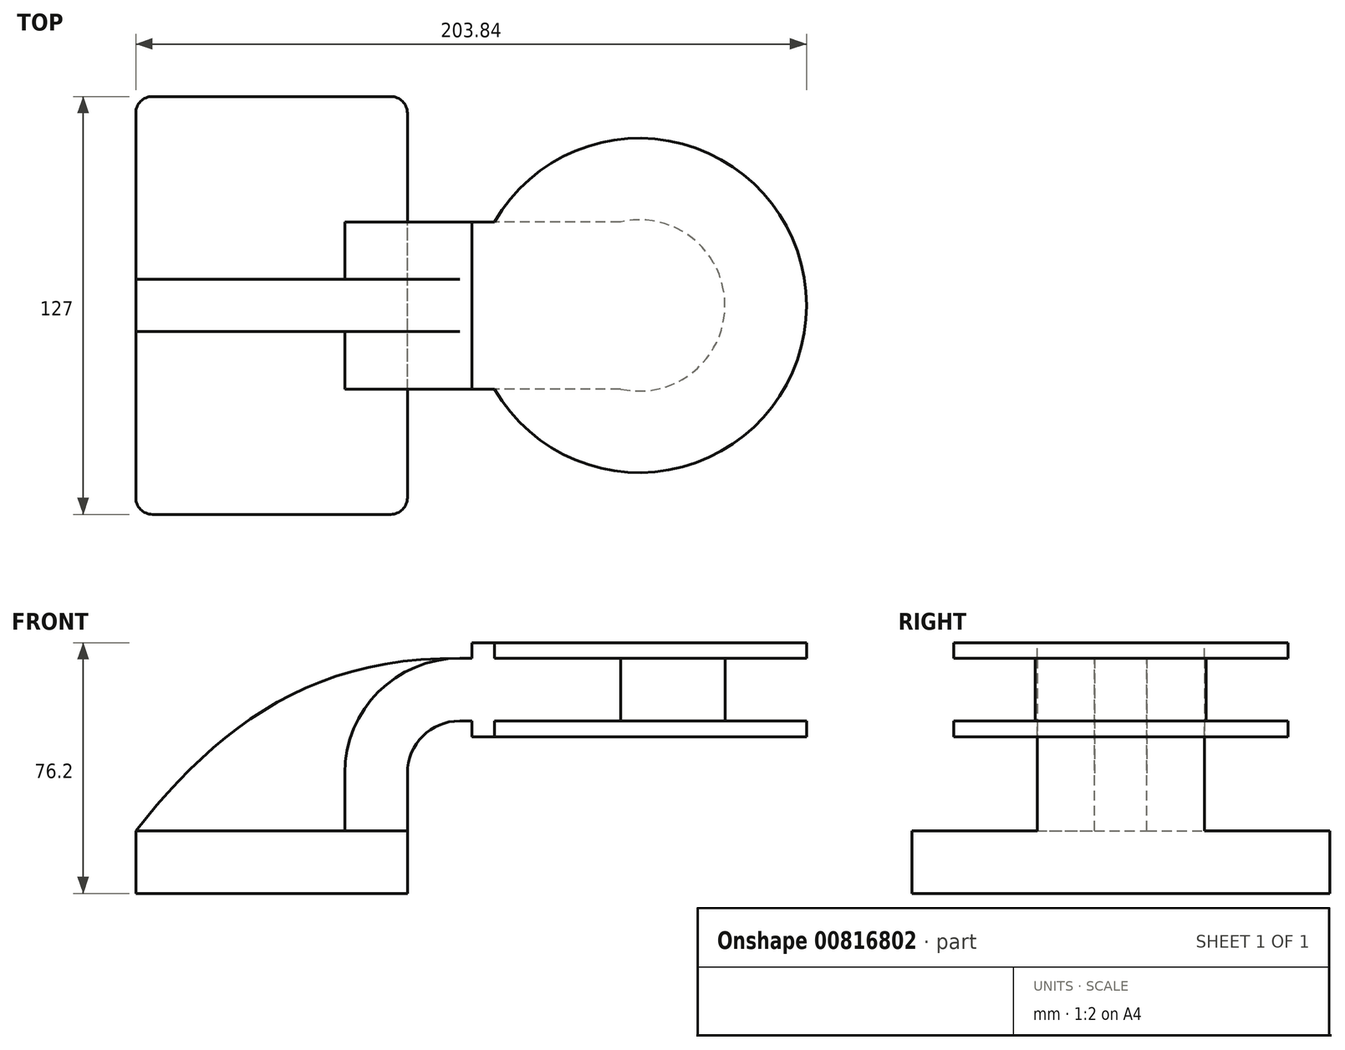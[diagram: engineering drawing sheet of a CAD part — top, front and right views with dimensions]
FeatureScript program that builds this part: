
annotation { "Feature Type Name" : "Feature", "Feature Type Description" : "" }
export const myFeature = defineFeature(function(context is Context, id is Id, definition is map)
    precondition{}
    {
        {
            var Q0;
            Q0=qCreatedBy(makeId("Front.planeOp"),FACE);
            var sketch = newSketch(context, id + "F0", { "sketchPlane" : qUnion([Q0])});
            skLineSegment(sketch, "E0.bottom", {"start": v(-41.28, 9.52) * mm, "end": v(41.27, 9.53) * mm});
            skLineSegment(sketch, "E0.top", {"start": v(-41.28, -9.53) * mm, "end": v(41.28, -9.53) * mm});
            skLineSegment(sketch, "E0.left", {"start": v(-41.28, 9.52) * mm, "end": v(-41.27, -9.53) * mm});
            skLineSegment(sketch, "E0.right", {"start": v(41.28, 9.53) * mm, "end": v(41.28, -9.52) * mm});
            skPoint(sketch, "E0.middle", {"position": v(0, 0) * mm});
            skLineSegment(sketch, "E1.bottom", {"start": v(60.96, 38.1) * mm, "end": v(111.76, 38.1) * mm});
            skLineSegment(sketch, "E1.top", {"start": v(60.96, 66.67) * mm, "end": v(111.76, 66.67) * mm});
            skLineSegment(sketch, "E1.left", {"start": v(60.96, 38.1) * mm, "end": v(60.96, 66.67) * mm});
            skLineSegment(sketch, "E1.right", {"start": v(111.76, 38.1) * mm, "end": v(111.76, 66.67) * mm});
            skPoint(sketch, "E1.middle", {"position": v(86.36, 52.39) * mm});
            skLineSegment(sketch, "E2", {"start": v(41.27, 9.53) * mm, "end": v(41.27, 27) * mm});
            skArc(sketch, "E3", {"start": v(57.15, 42.88) * mm, "mid": v(45.92, 38.23) * mm, "end": v(41.27, 27) * mm});
            skLineSegment(sketch, "E4", {"start": v(57.15, 42.88) * mm, "end": v(85.72, 42.88) * mm});
            skLineSegment(sketch, "E5.0", {"start": v(22.23, 9.53) * mm, "end": v(22.23, 27) * mm});
            skArc(sketch, "E5.1", {"start": v(57.15, 61.93) * mm, "mid": v(32.45, 51.7) * mm, "end": v(22.23, 27) * mm});
            skLineSegment(sketch, "E5.2", {"start": v(57.15, 61.93) * mm, "end": v(85.72, 61.93) * mm});
            skLineSegment(sketch, "E6", {"start": v(85.72, 66.67) * mm, "end": v(85.72, 38.1) * mm});
            skFitSpline(sketch, "E7", {"points": [v(-41.28, 9.52) * mm, v(57.15, 61.93) * mm], "startDerivative": vector(72.92, 91.6) * mm, "endDerivative": vector(139.33, -1.33) * mm});
            skSolve(sketch);
        }
        {
            var Q0;
            Q0=makeQuery(id+"F0.imprint","IMPRINT",FACE,{"disambiguationData":[TD([[makeQuery(id+"F0.imprint","IMPRINT",EDGE,{"derivedFrom":sQuery(id+"F0.wireOp",EDGE,"E0.top")}),1.0]])]});
            extrude(context, id + "F1", {"entities" : qUnion([Q0]), "endBound" : BoundingType.SYMMETRIC, "depth" : 127 * mm, "offsetDistance" : 25.4 * mm});
        }
        {
            var Q0;
            {var subQ1=sQuery(id+"F0.wireOp",EDGE,"E2");Q0=makeQuery(id+"F0.imprint","IMPRINT",FACE,{"disambiguationData":[TD([[makeQuery(id+"F0.imprint","IMPRINT",EDGE,{"derivedFrom":subQ1}),1.0]])]});}
            var Q1;
            {var subQ0=sQuery(id+"F0.wireOp",EDGE,"E4");var subQ1=sQuery(id+"F0.wireOp",EDGE,"E1.left");var subQ2=makeQuery(id+"F0.imprint","INTERSECT",VERTEX,{"derivedFrom":[subQ1,subQ0]});Q1=makeQuery(id+"F0.imprint","IMPRINT",FACE,{"disambiguationData":[TD([[makeQuery(id+"F0.imprint","IMPRINT",EDGE,{"disambiguationData":[TD([[subQ2,-1.0]])],"derivedFrom":subQ1}),-1.0]])]});}
            var Q2;
            {var subQ0=sQuery(id+"F0.wireOp",EDGE,"E1.left");var subQ1=sQuery(id+"F0.wireOp",EDGE,"E1.top");var subQ2=makeQuery(id+"F0.imprint","INTERSECT",VERTEX,{"derivedFrom":[subQ1,subQ0]});Q2=makeQuery(id+"F0.imprint","IMPRINT",FACE,{"disambiguationData":[TD([[makeQuery(id+"F0.imprint","IMPRINT",EDGE,{"disambiguationData":[TD([[subQ2,-1.0]])],"derivedFrom":subQ1}),-1.0]])]});}
            var Q3;
            {var subQ0=sQuery(id+"F0.wireOp",EDGE,"E1.left");var subQ1=sQuery(id+"F0.wireOp",EDGE,"E1.bottom");var subQ2=makeQuery(id+"F0.imprint","INTERSECT",VERTEX,{"derivedFrom":[subQ1,subQ0]});Q3=makeQuery(id+"F0.imprint","IMPRINT",FACE,{"disambiguationData":[TD([[makeQuery(id+"F0.imprint","IMPRINT",EDGE,{"disambiguationData":[TD([[subQ2,-1.0]])],"derivedFrom":subQ1}),1.0]])]});}
            var Q4;
            {var subQ0=sQuery(id+"F0.wireOp",EDGE,"E1.right");Q4=makeQuery(id+"F0.imprint","IMPRINT",FACE,{"disambiguationData":[TD([[makeQuery(id+"F0.imprint","IMPRINT",EDGE,{"derivedFrom":subQ0}),1.0]])]});}
            extrude(context, id + "F2", {"entities" : qUnion([Q0, Q1, Q2, Q3, Q4]), "operationType" : NewBodyOperationType.ADD, "endBound" : BoundingType.SYMMETRIC, "depth" : 50.8 * mm, "offsetDistance" : 25.4 * mm});
        }
        {
            var Q0;
            {var subQ2=sQuery(id+"F0.wireOp",EDGE,"E5.0");Q0=makeQuery(id+"F0.imprint","IMPRINT",FACE,{"disambiguationData":[TD([[makeQuery(id+"F0.imprint","IMPRINT",EDGE,{"derivedFrom":subQ2}),1.0]])]});}
            extrude(context, id + "F3", {"entities" : qUnion([Q0]), "operationType" : NewBodyOperationType.ADD, "endBound" : BoundingType.SYMMETRIC, "depth" : 15.88 * mm, "offsetDistance" : 25.4 * mm});
        }
        {
            var Q0;
            {var subQ0=sQuery(id+"F0.wireOp",EDGE,"E1.left");var subQ1=sQuery(id+"F0.wireOp",EDGE,"E1.top");var subQ2=makeQuery(id+"F0.imprint","INTERSECT",VERTEX,{"derivedFrom":[subQ1,subQ0]});Q0=makeQuery(id+"F0.imprint","IMPRINT",FACE,{"disambiguationData":[TD([[makeQuery(id+"F0.imprint","IMPRINT",EDGE,{"disambiguationData":[TD([[subQ2,-1.0]])],"derivedFrom":subQ1}),-1.0]])]});}
            var Q1;
            {var subQ0=sQuery(id+"F0.wireOp",EDGE,"E1.right");Q1=makeQuery(id+"F0.imprint","IMPRINT",FACE,{"disambiguationData":[TD([[makeQuery(id+"F0.imprint","IMPRINT",EDGE,{"derivedFrom":subQ0}),1.0]])]});}
            var Q2;
            {var subQ0=sQuery(id+"F0.wireOp",EDGE,"E1.left");var subQ1=sQuery(id+"F0.wireOp",EDGE,"E1.bottom");var subQ2=makeQuery(id+"F0.imprint","INTERSECT",VERTEX,{"derivedFrom":[subQ1,subQ0]});Q2=makeQuery(id+"F0.imprint","IMPRINT",FACE,{"disambiguationData":[TD([[makeQuery(id+"F0.imprint","IMPRINT",EDGE,{"disambiguationData":[TD([[subQ2,-1.0]])],"derivedFrom":subQ1}),1.0]])]});}
            var Q3;
            Q3=sQuery(id+"F0.wireOp",EDGE,"E1.right");
            revolve(context, id + "F4", {"operationType" : NewBodyOperationType.ADD, "surfaceOperationType" : NewSurfaceOperationType.NEW, "entities" : qUnion([Q0, Q1, Q2]), "axis" : qUnion([Q3]), "revolveType" : RevolveType.FULL});
        }
        {
            var Q0;
            Q0=makeQuery(id+"F1.opExtrude","CAP_EDGE",EDGE,{"disambiguationData":[OSD([sQuery(id+"F0.wireOp",EDGE,"E0.right")])],"isStart":false});
            var Q1;
            Q1=makeQuery(id+"F1.opExtrude","CAP_EDGE",EDGE,{"disambiguationData":[OSD([sQuery(id+"F0.wireOp",EDGE,"E0.left")])],"isStart":false});
            var Q2;
            Q2=makeQuery(id+"F1.opExtrude","CAP_EDGE",EDGE,{"disambiguationData":[OSD([sQuery(id+"F0.wireOp",EDGE,"E0.left")])],"isStart":true});
            var Q3;
            Q3=makeQuery(id+"F1.opExtrude","CAP_EDGE",EDGE,{"disambiguationData":[OSD([sQuery(id+"F0.wireOp",EDGE,"E0.right")])],"isStart":true});
            fillet(context, id + "F5", {"entities" : qUnion([Q0, Q1, Q2, Q3]), "radius" : 5.08 * mm, "tangentPropagation" : true, "allowEdgeOverflow" : false});
        }
    });
